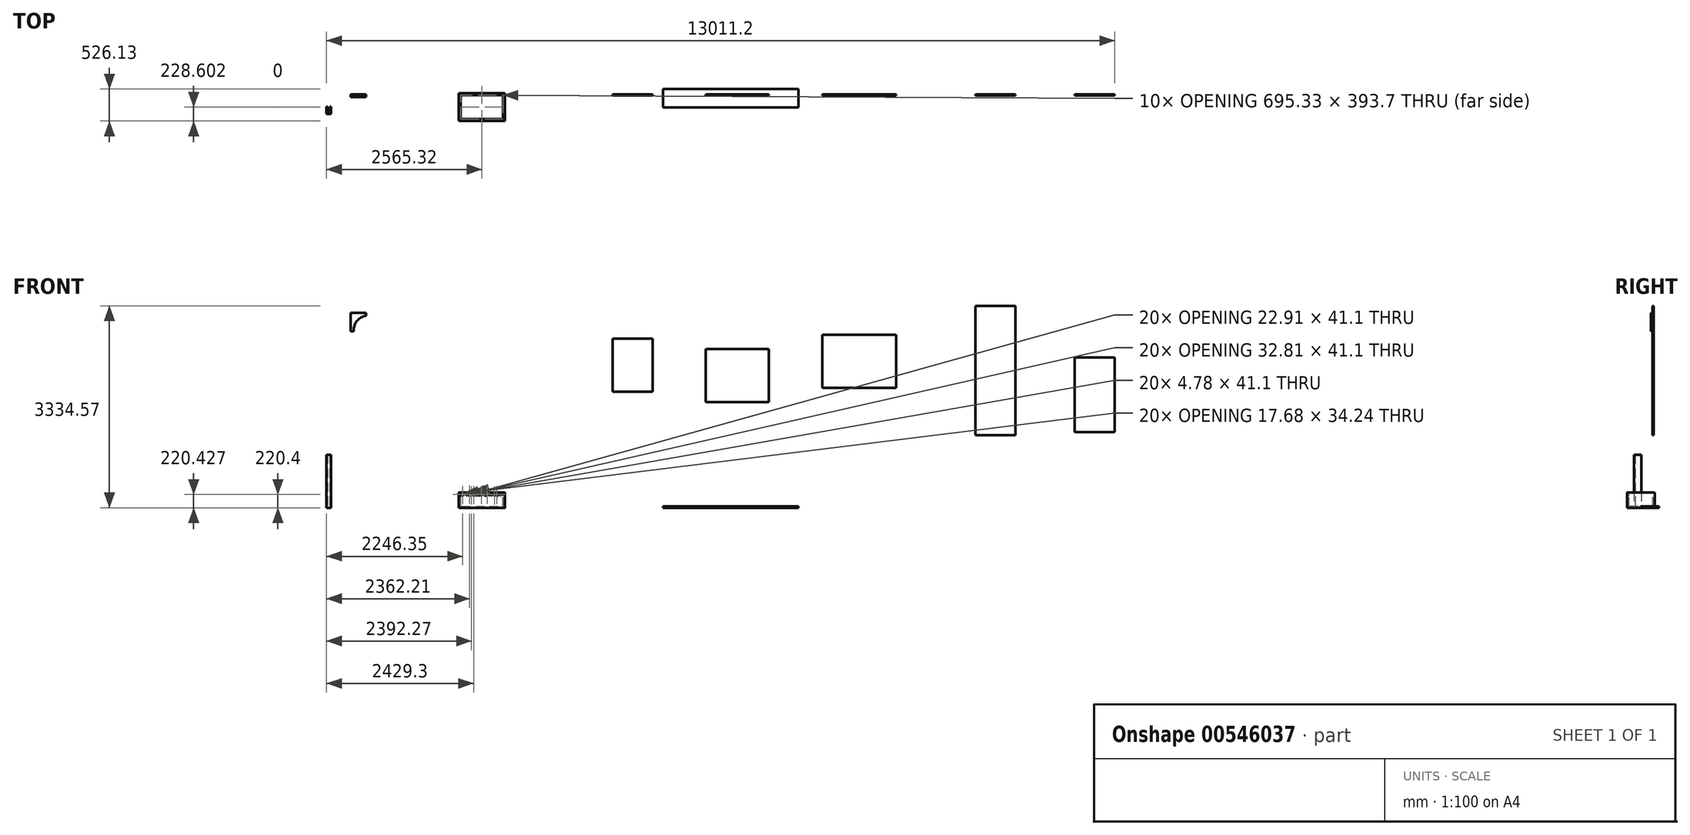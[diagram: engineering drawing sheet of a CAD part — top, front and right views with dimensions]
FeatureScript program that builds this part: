
annotation { "Feature Type Name" : "Feature", "Feature Type Description" : "" }
export const myFeature = defineFeature(function(context is Context, id is Id, definition is map)
    precondition{}
    {
        {
            var Q0;
            Q0=qCreatedBy(makeId("Top.planeOp"),FACE);
            var sketch = newSketch(context, id + "F0", { "sketchPlane" : qUnion([Q0])});
            skLineSegment(sketch, "E0.bottom", {"start": v(-734.13, 84.15) * mm, "end": v(1501.07, 84.15) * mm});
            skLineSegment(sketch, "E0.top", {"start": v(-734.13, -220.65) * mm, "end": v(1501.07, -220.65) * mm});
            skLineSegment(sketch, "E0.left", {"start": v(-734.13, 84.15) * mm, "end": v(-734.13, -220.65) * mm});
            skLineSegment(sketch, "E0.right", {"start": v(1501.07, 84.15) * mm, "end": v(1501.07, -220.65) * mm});
            skSolve(sketch);
        }
        {
            var Q0;
            Q0 = qSketchRegion(id + "F0", true);
            extrude(context, id + "F1", {"entities" : qUnion([Q0]), "depth" : 25.4 * mm, "offsetDistance" : 25.4 * mm});
        }
        {
            var Q0;
            Q0=qCreatedBy(makeId("Top.planeOp"),FACE);
            var sketch = newSketch(context, id + "F2", { "sketchPlane" : qUnion([Q0])});
            skLineSegment(sketch, "E1.bottom", {"start": v(-4105.8, 15.22) * mm, "end": v(-3343.8, 15.22) * mm});
            skLineSegment(sketch, "E1.top", {"start": v(-4105.8, -441.98) * mm, "end": v(-3343.8, -441.98) * mm});
            skLineSegment(sketch, "E1.left", {"start": v(-4105.8, 15.22) * mm, "end": v(-4105.8, -441.98) * mm});
            skLineSegment(sketch, "E1.right", {"start": v(-3343.8, 15.22) * mm, "end": v(-3343.8, -441.98) * mm});
            skSolve(sketch);
        }
        {
            var Q0;
            Q0 = qSketchRegion(id + "F2", true);
            extrude(context, id + "F3", {"entities" : qUnion([Q0]), "depth" : 254 * mm, "offsetDistance" : 25.4 * mm});
        }
        {
            var Q0;
            Q0=makeQuery(id+"F3.opExtrude","CAP_FACE",FACE,{"disambiguationData":[OSD([sQuery(id+"F2.wireOp",EDGE,"E1.bottom"),sQuery(id+"F2.wireOp",EDGE,"E1.top"),sQuery(id+"F2.wireOp",EDGE,"E1.left"),sQuery(id+"F2.wireOp",EDGE,"E1.right")])],"isStart":false});
            var sketch = newSketch(context, id + "F4", { "sketchPlane" : qUnion([Q0])});
            skLineSegment(sketch, "E2.bottom", {"start": v(-4072.46, -16.53) * mm, "end": v(-3377.13, -16.53) * mm});
            skLineSegment(sketch, "E2.top", {"start": v(-4072.46, -410.23) * mm, "end": v(-3377.13, -410.23) * mm});
            skLineSegment(sketch, "E2.left", {"start": v(-4072.46, -16.53) * mm, "end": v(-4072.46, -410.23) * mm});
            skLineSegment(sketch, "E2.right", {"start": v(-3377.13, -16.53) * mm, "end": v(-3377.13, -410.23) * mm});
            skLineSegment(sketch, "E3", {"start": v(-3377.13, -16.53) * mm, "end": v(-3343.8, -16.53) * mm, "construction": true});
            skLineSegment(sketch, "E4", {"start": v(-3377.13, -16.53) * mm, "end": v(-3377.13, 15.22) * mm, "construction": true});
            skLineSegment(sketch, "E5", {"start": v(-4072.46, -410.23) * mm, "end": v(-4105.8, -410.23) * mm, "construction": true});
            skLineSegment(sketch, "E6", {"start": v(-4072.46, -410.23) * mm, "end": v(-4072.46, -441.98) * mm, "construction": true});
            skSolve(sketch);
        }
        {
            var Q0;
            Q0 = qSketchRegion(id + "F4", true);
            extrude(context, id + "F5", {"entities" : qUnion([Q0]), "operationType" : NewBodyOperationType.REMOVE, "oppositeDirection" : true, "depth" : 228.6 * mm, "offsetDistance" : 25.4 * mm});
        }
        {
            var Q0;
            Q0=makeQuery(id+"F3.opExtrude","SWEPT_EDGE",EDGE,{"disambiguationData":[OSD([sQuery(id+"F2.wireOp",EDGE,"E1.top"),sQuery(id+"F2.wireOp",EDGE,"E1.left")])]});
            var Q1;
            Q1=makeQuery(id+"F3.opExtrude","SWEPT_EDGE",EDGE,{"disambiguationData":[OSD([sQuery(id+"F2.wireOp",EDGE,"E1.top"),sQuery(id+"F2.wireOp",EDGE,"E1.right")])]});
            var Q2;
            Q2=makeQuery(id+"F3.opExtrude","SWEPT_EDGE",EDGE,{"disambiguationData":[OSD([sQuery(id+"F2.wireOp",EDGE,"E1.bottom"),sQuery(id+"F2.wireOp",EDGE,"E1.right")])]});
            var Q3;
            Q3=makeQuery(id+"F3.opExtrude","SWEPT_EDGE",EDGE,{"disambiguationData":[OSD([sQuery(id+"F2.wireOp",EDGE,"E1.bottom"),sQuery(id+"F2.wireOp",EDGE,"E1.left")])]});
            var Q4;
            Q4=makeQuery(id+"F3.opExtrude","CAP_EDGE",EDGE,{"disambiguationData":[OSD([sQuery(id+"F2.wireOp",EDGE,"E1.bottom")])],"isStart":false});
            var Q5;
            Q5=makeQuery(id+"F3.opExtrude","CAP_EDGE",EDGE,{"disambiguationData":[OSD([sQuery(id+"F2.wireOp",EDGE,"E1.left")])],"isStart":false});
            var Q6;
            Q6=makeQuery(id+"F3.opExtrude","CAP_EDGE",EDGE,{"disambiguationData":[OSD([sQuery(id+"F2.wireOp",EDGE,"E1.top")])],"isStart":false});
            var Q7;
            Q7=makeQuery(id+"F3.opExtrude","CAP_EDGE",EDGE,{"disambiguationData":[OSD([sQuery(id+"F2.wireOp",EDGE,"E1.right")])],"isStart":false});
            var Q8;
            Q8=makeQuery(id+"F5.boolean.opBoolean","COPY",EDGE,{"derivedFrom":makeQuery(id+"F5.opExtrude","CAP_EDGE",EDGE,{"disambiguationData":[OSD([sQuery(id+"F4.wireOp",EDGE,"E2.right")])],"isStart":true})});
            var Q9;
            Q9=makeQuery(id+"F5.boolean.opBoolean","COPY",EDGE,{"derivedFrom":makeQuery(id+"F5.opExtrude","CAP_EDGE",EDGE,{"disambiguationData":[OSD([sQuery(id+"F4.wireOp",EDGE,"E2.top")])],"isStart":true})});
            var Q10;
            Q10=makeQuery(id+"F5.boolean.opBoolean","COPY",EDGE,{"derivedFrom":makeQuery(id+"F5.opExtrude","CAP_EDGE",EDGE,{"disambiguationData":[OSD([sQuery(id+"F4.wireOp",EDGE,"E2.bottom")])],"isStart":true})});
            var Q11;
            Q11=makeQuery(id+"F5.boolean.opBoolean","COPY",EDGE,{"derivedFrom":makeQuery(id+"F5.opExtrude","CAP_EDGE",EDGE,{"disambiguationData":[OSD([sQuery(id+"F4.wireOp",EDGE,"E2.left")])],"isStart":true})});
            var Q12;
            Q12=makeQuery(id+"F5.boolean.opBoolean","COPY",EDGE,{"derivedFrom":makeQuery(id+"F5.opExtrude","SWEPT_EDGE",EDGE,{"disambiguationData":[OSD([sQuery(id+"F4.wireOp",EDGE,"E2.bottom"),sQuery(id+"F4.wireOp",EDGE,"E2.left")])]})});
            var Q13;
            Q13=makeQuery(id+"F5.boolean.opBoolean","COPY",EDGE,{"derivedFrom":makeQuery(id+"F5.opExtrude","SWEPT_EDGE",EDGE,{"disambiguationData":[OSD([sQuery(id+"F4.wireOp",EDGE,"E2.top"),sQuery(id+"F4.wireOp",EDGE,"E2.left")])]})});
            var Q14;
            Q14=makeQuery(id+"F5.boolean.opBoolean","COPY",EDGE,{"derivedFrom":makeQuery(id+"F5.opExtrude","SWEPT_EDGE",EDGE,{"disambiguationData":[OSD([sQuery(id+"F4.wireOp",EDGE,"E2.top"),sQuery(id+"F4.wireOp",EDGE,"E2.right")])]})});
            var Q15;
            Q15=makeQuery(id+"F5.boolean.opBoolean","COPY",EDGE,{"derivedFrom":makeQuery(id+"F5.opExtrude","SWEPT_EDGE",EDGE,{"disambiguationData":[OSD([sQuery(id+"F4.wireOp",EDGE,"E2.bottom"),sQuery(id+"F4.wireOp",EDGE,"E2.right")])]})});
            fillet(context, id + "F6", {"entities" : qUnion([Q0, Q1, Q2, Q3, Q4, Q5, Q6, Q7, Q8, Q9, Q10, Q11, Q12, Q13, Q14, Q15]), "radius" : 12.7 * mm, "tangentPropagation" : true, "allowEdgeOverflow" : false});
        }
        {
            var Q0;
            Q0=makeQuery(id+"F3.opExtrude","SWEPT_FACE",FACE,{"disambiguationData":[OSD([sQuery(id+"F2.wireOp",EDGE,"E1.top")])]});
            var sketch = newSketch(context, id + "F7", { "sketchPlane" : qUnion([Q0])});
            skText(sketch, "E7", { "text": "30\" WIDE X 10\" SINK DEPTH", "fontName": "OpenSans-Regular.ttf"});
            const initialGuessF7  = {"E7": [-4.0931, 0.19985, 1, 0, 0.04145]};
            skSetInitialGuess(sketch, initialGuessF7);
            skSolve(sketch);
        }
        {
            var Q0;
            Q0 = qSketchRegion(id + "F7", true);
            extrude(context, id + "F8", {"entities" : qUnion([Q0]), "operationType" : NewBodyOperationType.REMOVE, "oppositeDirection" : true, "depth" : 25.4 * mm, "offsetDistance" : 25.4 * mm});
        }
        {
            var Q0;
            Q0=qCreatedBy(makeId("Top.planeOp"),FACE);
            var sketch = newSketch(context, id + "F9", { "sketchPlane" : qUnion([Q0])});
            skLineSegment(sketch, "E8.bottom", {"start": v(-6290.11, -307.7) * mm, "end": v(-6213.91, -307.7) * mm});
            skLineSegment(sketch, "E8.top", {"start": v(-6290.11, -326.76) * mm, "end": v(-6213.91, -326.76) * mm});
            skLineSegment(sketch, "E8.left", {"start": v(-6290.11, -307.7) * mm, "end": v(-6290.11, -326.76) * mm});
            skLineSegment(sketch, "E8.right", {"start": v(-6213.91, -307.7) * mm, "end": v(-6213.91, -326.76) * mm});
            skSolve(sketch);
        }
        {
            var Q0;
            Q0 = qSketchRegion(id + "F9", true);
            extrude(context, id + "F10", {"entities" : qUnion([Q0]), "depth" : 876.3 * mm, "offsetDistance" : 25.4 * mm});
        }
        {
            var Q0;
            Q0=makeQuery(id+"F10.opExtrude","SWEPT_FACE",FACE,{"disambiguationData":[OSD([sQuery(id+"F9.wireOp",EDGE,"E8.bottom")])]});
            var sketch = newSketch(context, id + "F11", { "sketchPlane" : qUnion([Q0])});
            skLineSegment(sketch, "E9.bottom", {"start": v(6290.11, 876.3) * mm, "end": v(6271.06, 876.3) * mm});
            skLineSegment(sketch, "E9.top", {"start": v(6290.11, 0) * mm, "end": v(6271.06, 0) * mm});
            skLineSegment(sketch, "E9.left", {"start": v(6290.11, 876.3) * mm, "end": v(6290.11, 0) * mm});
            skLineSegment(sketch, "E9.right", {"start": v(6271.06, 876.3) * mm, "end": v(6271.06, 0) * mm});
            skLineSegment(sketch, "E10.bottom", {"start": v(6213.91, 876.3) * mm, "end": v(6232.96, 876.3) * mm});
            skLineSegment(sketch, "E10.top", {"start": v(6213.91, 0) * mm, "end": v(6232.96, 0) * mm});
            skLineSegment(sketch, "E10.left", {"start": v(6213.91, 876.3) * mm, "end": v(6213.91, 0) * mm});
            skLineSegment(sketch, "E10.right", {"start": v(6232.96, 876.3) * mm, "end": v(6232.96, 0) * mm});
            skSolve(sketch);
        }
        {
            var Q0;
            Q0 = qSketchRegion(id + "F11", true);
            extrude(context, id + "F12", {"entities" : qUnion([Q0]), "operationType" : NewBodyOperationType.ADD, "depth" : 101.6 * mm, "offsetDistance" : 25.4 * mm});
        }
        {
            var Q0;
            Q0=qCreatedBy(makeId("Front.planeOp"),FACE);
            var sketch = newSketch(context, id + "F13", { "sketchPlane" : qUnion([Q0])});
            skLineSegment(sketch, "E11", {"start": v(-5890.24, 3220.74) * mm, "end": v(-5636.24, 3220.74) * mm});
            skLineSegment(sketch, "E12", {"start": v(-5890.24, 3220.74) * mm, "end": v(-5890.24, 2915.94) * mm});
            skLineSegment(sketch, "E13", {"start": v(-5890.24, 2915.94) * mm, "end": v(-5839.44, 2915.94) * mm});
            skLineSegment(sketch, "E14", {"start": v(-5636.24, 3220.74) * mm, "end": v(-5636.24, 3169.94) * mm});
            skArc(sketch, "E15", {"start": v(-5636.24, 3169.94) * mm, "mid": v(-5787.77, 3082.88) * mm, "end": v(-5839.44, 2915.94) * mm});
            skSolve(sketch);
        }
        {
            var Q0;
            Q0 = qSketchRegion(id + "F13", true);
            extrude(context, id + "F14", {"entities" : qUnion([Q0]), "depth" : 44.45 * mm, "offsetDistance" : 25.4 * mm});
        }
        {
            var Q0;
            Q0=qCreatedBy(makeId("Front.planeOp"),FACE);
            var sketch = newSketch(context, id + "F15", { "sketchPlane" : qUnion([Q0])});
            skLineSegment(sketch, "E16.bottom", {"start": v(-1565.52, 2794) * mm, "end": v(-905.12, 2794) * mm});
            skLineSegment(sketch, "E16.top", {"start": v(-1565.52, 1917.7) * mm, "end": v(-905.12, 1917.7) * mm});
            skLineSegment(sketch, "E16.left", {"start": v(-1565.52, 2794) * mm, "end": v(-1565.52, 1917.7) * mm});
            skLineSegment(sketch, "E16.right", {"start": v(-905.12, 2794) * mm, "end": v(-905.12, 1917.7) * mm});
            skSolve(sketch);
        }
        {
            var Q0;
            Q0 = qSketchRegion(id + "F15", true);
            extrude(context, id + "F16", {"entities" : qUnion([Q0]), "depth" : 19.05 * mm, "offsetDistance" : 25.4 * mm});
        }
        {
            var Q0;
            Q0=qCreatedBy(makeId("Front.planeOp"),FACE);
            var sketch = newSketch(context, id + "F17", { "sketchPlane" : qUnion([Q0])});
            skLineSegment(sketch, "E17.bottom", {"start": v(-29.47, 2619.03) * mm, "end": v(1011.93, 2619.03) * mm});
            skLineSegment(sketch, "E17.top", {"start": v(-29.47, 1742.73) * mm, "end": v(1011.93, 1742.73) * mm});
            skLineSegment(sketch, "E17.left", {"start": v(-29.47, 2619.03) * mm, "end": v(-29.47, 1742.73) * mm});
            skLineSegment(sketch, "E17.right", {"start": v(1011.93, 2619.03) * mm, "end": v(1011.93, 1742.73) * mm});
            skSolve(sketch);
        }
        {
            var Q0;
            Q0 = qSketchRegion(id + "F17", true);
            extrude(context, id + "F18", {"entities" : qUnion([Q0]), "depth" : 19.05 * mm, "offsetDistance" : 25.4 * mm});
        }
        {
            var Q0;
            Q0=qCreatedBy(makeId("Front.planeOp"),FACE);
            var sketch = newSketch(context, id + "F19", { "sketchPlane" : qUnion([Q0])});
            skLineSegment(sketch, "E18.bottom", {"start": v(1893.8, 2858.7) * mm, "end": v(3113, 2858.7) * mm});
            skLineSegment(sketch, "E18.top", {"start": v(1893.8, 1982.4) * mm, "end": v(3113, 1982.4) * mm});
            skLineSegment(sketch, "E18.left", {"start": v(1893.8, 2858.7) * mm, "end": v(1893.8, 1982.4) * mm});
            skLineSegment(sketch, "E18.right", {"start": v(3113, 2858.7) * mm, "end": v(3113, 1982.4) * mm});
            skSolve(sketch);
        }
        {
            var Q0;
            Q0 = qSketchRegion(id + "F19", true);
            extrude(context, id + "F20", {"entities" : qUnion([Q0]), "depth" : 19.05 * mm, "offsetDistance" : 25.4 * mm});
        }
        {
            var Q0;
            Q0=qCreatedBy(makeId("Front.planeOp"),FACE);
            var sketch = newSketch(context, id + "F21", { "sketchPlane" : qUnion([Q0])});
            skLineSegment(sketch, "E19.bottom", {"start": v(4420.45, 3334.57) * mm, "end": v(5080.85, 3334.57) * mm});
            skLineSegment(sketch, "E19.top", {"start": v(4420.45, 1200.97) * mm, "end": v(5080.85, 1200.97) * mm});
            skLineSegment(sketch, "E19.left", {"start": v(4420.45, 3334.57) * mm, "end": v(4420.45, 1200.97) * mm});
            skLineSegment(sketch, "E19.right", {"start": v(5080.85, 3334.57) * mm, "end": v(5080.85, 1200.97) * mm});
            skSolve(sketch);
        }
        {
            var Q0;
            Q0 = qSketchRegion(id + "F21", true);
            extrude(context, id + "F22", {"entities" : qUnion([Q0]), "depth" : 19.05 * mm, "offsetDistance" : 25.4 * mm});
        }
        {
            var Q0;
            Q0=qCreatedBy(makeId("Front.planeOp"),FACE);
            var sketch = newSketch(context, id + "F23", { "sketchPlane" : qUnion([Q0])});
            skLineSegment(sketch, "E20.bottom", {"start": v(6060.7, 2483.43) * mm, "end": v(6721.1, 2483.43) * mm});
            skLineSegment(sketch, "E20.top", {"start": v(6060.7, 1251.53) * mm, "end": v(6721.1, 1251.53) * mm});
            skLineSegment(sketch, "E20.left", {"start": v(6060.7, 2483.43) * mm, "end": v(6060.7, 1251.53) * mm});
            skLineSegment(sketch, "E20.right", {"start": v(6721.1, 2483.43) * mm, "end": v(6721.1, 1251.53) * mm});
            skSolve(sketch);
        }
        {
            var Q0;
            Q0 = qSketchRegion(id + "F23", true);
            extrude(context, id + "F24", {"entities" : qUnion([Q0]), "depth" : 19.05 * mm, "offsetDistance" : 25.4 * mm});
        }
    });
